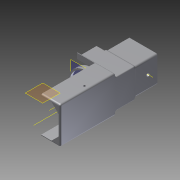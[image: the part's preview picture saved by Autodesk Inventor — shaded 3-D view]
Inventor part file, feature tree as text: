
AUTODESK INVENTOR PART (.ipt)
format: ipt  version: 2012 (Build 160160000, 160)  size: 886,784 bytes
history: native  units: mm
features: sketch x30, extrude x30, reference x30, projected_geometry x23, fillet x12, plane x5, other x3
ambient origin geometry x8: Origin, YZ Plane, XZ Plane, XY Plane, X Axis, Y Axis, Z Axis, Center Point
bodies: Solid1 (feature_tree)
feature tree (133):
  plane  "Work Plane2"
  sketch  "Sketch3"  dims[d1=0.3mm d2=0.3mm]
  plane  "Work Plane3"
  extrude  "Extrusion1"  Depth=0.3mm
  extrude  "Extrusion2"  Depth=10.0mm TaperAngle=0.0deg
  plane  "Work Plane4"
  extrude  "Extrusion3"  Depth=10.0mm TaperAngle=0.0deg
  extrude  "Extrusion4"  Depth=2.0mm
  extrude  "Extrusion5"  Depth=2.0mm
  extrude  "Extrusion6"  Depth=2.0mm TaperAngle=0.0deg
  extrude  "Extrusion7"  TaperAngle=0.0deg  [1 undecoded]
  extrude  "Extrusion8"  TaperAngle=0.0deg  [1 undecoded]
  fillet  "Fillet3"  Radius=20.0mm
  fillet  "Fillet4"  Radius=20.0mm
  fillet  "Fillet5"  Radius=0.3mm
  extrude  "Extrusion10"  Depth=0.3mm
  extrude  "Extrusion11"  Depth=0.3mm TaperAngle=0.0deg
  extrude  "Extrusion12"  Depth=1.0mm
  extrude  "Extrusion13"  Depth=2.0mm TaperAngle=0.0deg
  extrude  "Extrusion14"  Depth=0.3mm
  extrude  "Extrusion15"  Depth=0.3mm
  extrude  "Extrusion16"  TaperAngle=0.0deg  [1 undecoded]
  extrude  "Extrusion17"  Depth=2.0mm
  extrude  "Extrusion18"  Depth=2.0mm TaperAngle=0.0deg
  extrude  "Extrusion20"  Depth=14.0mm
  extrude  "Extrusion21"  Depth=7.0mm TaperAngle=0.0deg
  plane  "Work Plane5"
  extrude  "Extrusion22"  Depth=3.3mm
  extrude  "Extrusion23"  Depth=3.3mm
  extrude  "Extrusion24"  Depth=0.3mm
  extrude  "Extrusion25"  Depth=0.3mm
  plane  "Work Plane7"
  extrude  "Extrusion26"  Depth=20.0mm TaperAngle=0.0deg
  extrude  "Extrusion27"  Depth=0.3mm
  extrude  "Extrusion28"  Depth=0.3mm
  extrude  "Extrusion29"  Depth=2.0mm
  extrude  "Extrusion30"  Depth=2.0mm
  extrude  "Extrusion31"  TaperAngle=45.0deg  [1 undecoded]
  extrude  "Extrusion34"  Depth=9.0mm
  other  "Work Axis1"
  other  "Work Axis2"
  fillet  "Fillet47"  Radius=10.0mm
  fillet  "Fillet48"  [1 undecoded]
  fillet  "Fillet49"  Radius=10.0mm
  fillet  "Fillet50"  Radius=10.0mm
  fillet  "Fillet51"  Radius=10.0mm
  fillet  "Fillet52"  Radius=0.3mm
  fillet  "Fillet53"  Radius=0.3mm
  fillet  "Fillet54"  Radius=10.0mm
  fillet  "Fillet55"  Radius=10.0mm
  other  "Work Axis3"
  reference  "Reference32"
  sketch  "Sketch4"  dims[d3=2.0mm d4=10.0mm d5=0.0mm]
  reference  "Reference33"
  sketch  "Sketch5"  dims[d6=0.3mm d7=10.0mm d8=0.0mm]
  sketch  "Sketch7"  dims[d9=2.0mm d10=2.0mm]
  projected_geometry  "Projected Loop3"
  sketch  "Sketch8"  dims[d11=2.0mm d12=2.0mm]
  sketch  "Sketch10"  dims[d13=120.0mm d14=2.0mm d15=0.0mm]
  reference  "Reference36"
  sketch  "Sketch11"  dims[d24=2.0mm d25=0.0mm]
  reference  "Reference37"
  sketch  "Sketch12"  dims[d26=2.0mm d27=0.0mm d28=20.0mm d29=0.0mm d31=20.0mm d32=0.0mm d34=0.3mm]
  sketch  "Sketch15"  dims[d35=20.0mm d36=0.0mm d37=0.3mm]
  projected_geometry  "Projected Loop5"
  projected_geometry  "Projected Loop6"
  sketch  "Sketch16"  dims[d38=10.0mm d39=0.0mm d40=0.3mm d41=0.0mm]
  reference  "Reference46"
  reference  "Reference47"
  reference  "Reference48"
  reference  "Reference49"
  reference  "Reference50"
  reference  "Reference51"
  reference  "Reference52"
  reference  "Reference53"
  sketch  "Sketch17"  dims[d43=1.0mm d44=1.0mm]
  reference  "Reference54"
  reference  "Reference55"
  reference  "Reference56"
  reference  "Reference57"
  reference  "Reference58"
  reference  "Reference59"
  reference  "Reference60"
  reference  "Reference61"
  sketch  "Sketch18"  dims[d45=1.0mm d52=2.0mm d53=0.0mm]
  reference  "Reference62"
  sketch  "Sketch19"  dims[d58=2.0mm d59=0.0mm d60=0.3mm]
  projected_geometry  "Projected Loop7"
  projected_geometry  "Projected Loop8"
  sketch  "Sketch20"  dims[d61=0.3mm d62=0.3mm]
  projected_geometry  "Projected Loop9"
  projected_geometry  "Projected Loop10"
  sketch  "Sketch21"  dims[d63=0.3mm d64=0.0mm]
  projected_geometry  "Projected Loop11"
  sketch  "Sketch22"  dims[d66=0.0mm d67=2.0mm]
  reference  "Reference63"
  reference  "Reference64"
  reference  "Reference65"
  reference  "Reference66"
  reference  "Reference67"
  reference  "Reference68"
  reference  "Reference69"
  reference  "Reference70"
  sketch  "Sketch23"  dims[d68=2.0mm d69=2.0mm d70=0.0mm]
  projected_geometry  "Projected Loop12"
  projected_geometry  "Projected Loop13"
  projected_geometry  "Projected Loop14"
  projected_geometry  "Projected Loop15"
  sketch  "Sketch25"  dims[d72=2.0mm d73=0.0mm d74=14.0mm]
  projected_geometry  "Projected Loop16"
  sketch  "Sketch26"  dims[d78=2.0mm d79=0.0mm d80=7.0mm d81=0.0mm]
  sketch  "Sketch28"  dims[d82=10.0mm d83=0.0mm d84=3.3mm]
  projected_geometry  "Projected Loop21"
  sketch  "Sketch29"  dims[d85=3.3mm d86=3.3mm]
  projected_geometry  "Projected Loop22"
  projected_geometry  "Projected Loop23"
  sketch  "Sketch30"  dims[d87=3.3mm d88=0.3mm]
  projected_geometry  "Projected Loop24"
  sketch  "Sketch31"  dims[d89=0.3mm d90=0.3mm]
  projected_geometry  "Projected Loop25"
  sketch  "Sketch32"  dims[d91=0.3mm d94=20.0mm d95=0.0mm]
  sketch  "Sketch33"  dims[d97=0.3mm d98=0.3mm]
  projected_geometry  "Projected Loop26"
  sketch  "Sketch34"  dims[d99=0.3mm d100=0.3mm]
  projected_geometry  "Projected Loop27"
  sketch  "Sketch35"  dims[d101=0.3mm d102=0.0mm d103=2.0mm]
  projected_geometry  "Projected Loop28"
  projected_geometry  "Projected Loop29"
  sketch  "Sketch37"  dims[d104=2.0mm d105=2.0mm]
  sketch  "Sketch38"  dims[d106=2.0mm d111=45.0deg]
  projected_geometry  "Projected Loop31"
  sketch  "Sketch41"  dims[d112=9.0mm d113=9.0mm d114=10.0mm d115=0.0mm d116=0.0mm d117=0.0mm d123=10.0mm d124=0.0mm d132=10.0mm d133=0.0mm d134=10.0mm d135=0.0mm d138=0.3mm d139=0.0mm d151=0.3mm d152=0.0mm d153=10.0mm d154=0.0mm d155=10.0mm d156=0.0mm d157=10.0mm d158=0.0mm d159=4.0mm d160=10.0mm d161=0.0mm d162=10.0mm d163=0.0mm d186=25.4mm d187=0.0mm d189=1.0mm d190=2.0mm d191=2.0mm d192=2.0mm d193=2.0mm d194=1.0mm d195=2.0mm d196=2.0mm d197=1.5mm]
  reference  "Reference73"
note: 5 required parameter values undecoded (feature->parameter linkage not recoverable at this tier; creation-order binding heuristic only, values carry confidence <= 0.55)
